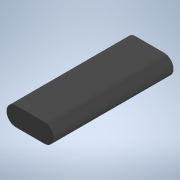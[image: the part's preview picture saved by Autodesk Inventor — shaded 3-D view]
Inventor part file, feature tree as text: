
AUTODESK INVENTOR PART (.ipt)
format: ipt  version: 2022 (Build 260153000, 153)  size: 95,232 bytes
history: native  units: in
note: dims shown in document units (in); Inventor stores cm internally (conversion verified against a paired STEP export)
features: extrude x1, sketch x1
ambient origin geometry x8: Origin, YZ Plane, XZ Plane, XY Plane, X Axis, Y Axis, Z Axis, Center Point
bodies: Solid1 (feature_tree)
feature tree (2):
  extrude  "Extrusion1"  Depth=0.875in
  sketch  "Sketch1"  dims[d0=0.1575in d1=0.2362in d2=0.875in d3=0.0in]
